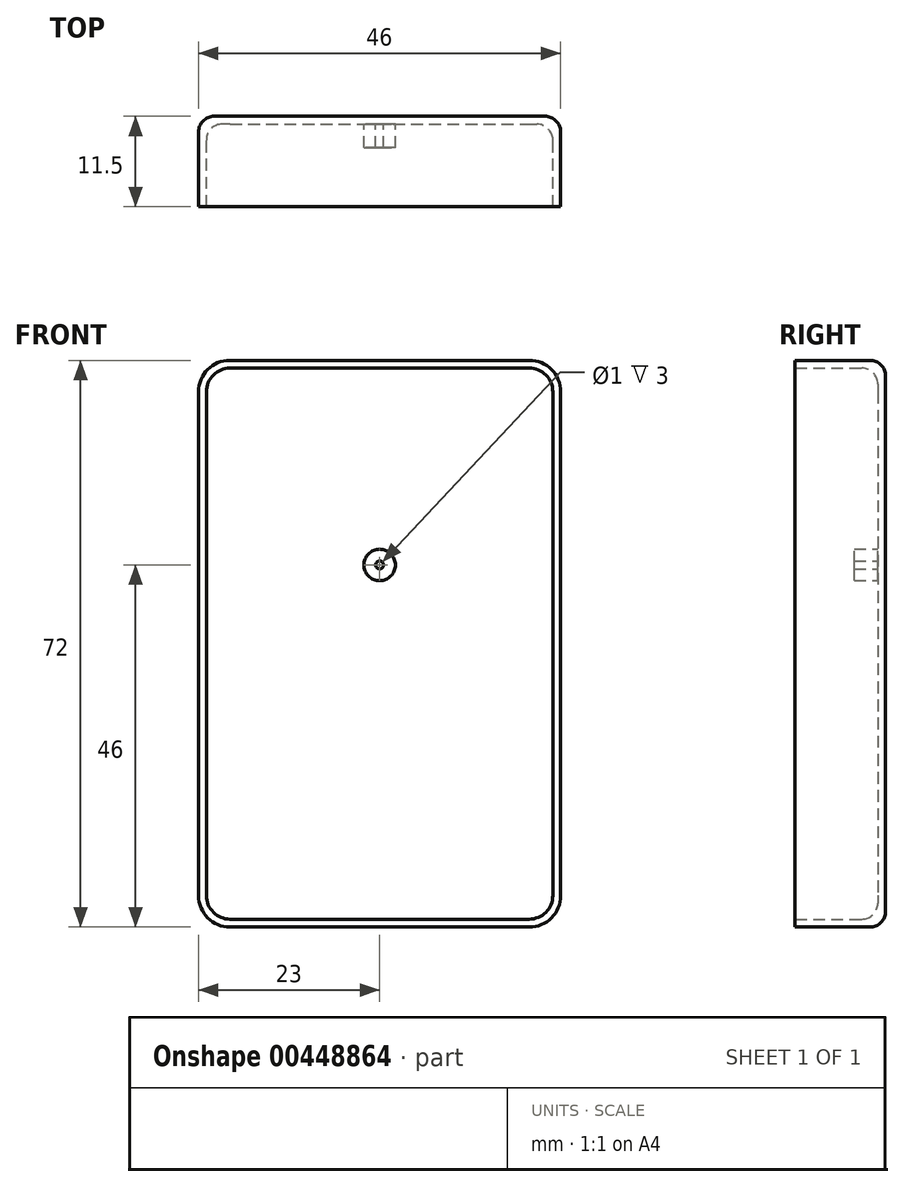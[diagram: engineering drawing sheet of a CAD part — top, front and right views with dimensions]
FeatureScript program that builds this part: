
annotation { "Feature Type Name" : "Feature", "Feature Type Description" : "" }
export const myFeature = defineFeature(function(context is Context, id is Id, definition is map)
    precondition{}
    {
        {
            var Q0;
            Q0=qCreatedBy(makeId("Front.planeOp"),FACE);
            var sketch = newSketch(context, id + "F0", { "sketchPlane" : qUnion([Q0])});
            skLineSegment(sketch, "E0.bottom", {"start": v(-19, 36) * mm, "end": v(19, 36) * mm});
            skLineSegment(sketch, "E0.top", {"start": v(-19, -36) * mm, "end": v(19, -36) * mm});
            skLineSegment(sketch, "E0.left", {"start": v(-23, 32) * mm, "end": v(-23, -32) * mm});
            skLineSegment(sketch, "E0.right", {"start": v(23, 32) * mm, "end": v(23, -32) * mm});
            skPoint(sketch, "E0.middle", {"position": v(0, 0) * mm});
            skPoint(sketch, "E1.visualSharp", {"position": v(23, 36) * mm});
            skArc(sketch, "E1.filletArc", {"start": v(23, 32) * mm, "mid": v(21.83, 34.83) * mm, "end": v(19, 36) * mm});
            skPoint(sketch, "E2.visualSharp", {"position": v(-23, 36) * mm});
            skArc(sketch, "E2.filletArc", {"start": v(-19, 36) * mm, "mid": v(-21.83, 34.83) * mm, "end": v(-23, 32) * mm});
            skPoint(sketch, "E3.visualSharp", {"position": v(-23, -36) * mm});
            skArc(sketch, "E3.filletArc", {"start": v(-23, -32) * mm, "mid": v(-21.83, -34.83) * mm, "end": v(-19, -36) * mm});
            skPoint(sketch, "E4.visualSharp", {"position": v(23, -36) * mm});
            skArc(sketch, "E4.filletArc", {"start": v(19, -36) * mm, "mid": v(21.83, -34.83) * mm, "end": v(23, -32) * mm});
            skSolve(sketch);
        }
        {
            var Q0;
            Q0=makeQuery(id+"F0.imprint","IMPRINT",FACE,{"disambiguationData":[TD([[makeQuery(id+"F0.imprint","IMPRINT",EDGE,{"derivedFrom":sQuery(id+"F0.wireOp",EDGE,"E0.bottom")}),-1.0]])]});
            extrude(context, id + "F1", {"entities" : qUnion([Q0]), "depth" : 11.5 * mm});
        }
        {
            var Q0;
            Q0=makeQuery(id+"F1.opExtrude","CAP_FACE",FACE,{"disambiguationData":[OSD([sQuery(id+"F0.wireOp",EDGE,"E0.bottom"),sQuery(id+"F0.wireOp",EDGE,"E0.top"),sQuery(id+"F0.wireOp",EDGE,"E0.left"),sQuery(id+"F0.wireOp",EDGE,"E0.right"),sQuery(id+"F0.wireOp",EDGE,"E1.filletArc"),sQuery(id+"F0.wireOp",EDGE,"E2.filletArc"),sQuery(id+"F0.wireOp",EDGE,"E3.filletArc"),sQuery(id+"F0.wireOp",EDGE,"E4.filletArc")])],"isStart":false});
            shell(context, id + "F2", {"entities" : qUnion([Q0]), "thickness" : 1 * mm});
        }
        {
            var Q0;
            Q0=qCreatedBy(makeId("Front.planeOp"),FACE);
            var sketch = newSketch(context, id + "F3", { "sketchPlane" : qUnion([Q0])});
            skCircle(sketch, "E5", {"center": v(0, 10) * mm, "radius": 2 * mm});
            skCircle(sketch, "E6", {"center": v(0, 10) * mm, "radius": 0.5 * mm});
            skSolve(sketch);
        }
        {
            var Q0;
            Q0 = qSketchRegion(id + "F3", true);
            extrude(context, id + "F4", {"entities" : qUnion([Q0]), "operationType" : NewBodyOperationType.ADD, "depth" : 4 * mm});
        }
        {
            var Q0;
            Q0=makeQuery(id+"F1.opExtrude","CAP_EDGE",EDGE,{"disambiguationData":[OSD([sQuery(id+"F0.wireOp",EDGE,"E0.right")])],"isStart":true});
            var Q1;
            {var subQ0=sQuery(id+"F0.wireOp",EDGE,"E0.left");Q1=makeQuery(id+"F2.opShell","OFFSET_EDGE",EDGE,{"disambiguationData":[OSD([subQ0]),TDD([makeQuery(id+"F1.opExtrude","CAP_EDGE",EDGE,{"disambiguationData":[OSD([subQ0])],"isStart":true})])]});}
            fillet(context, id + "F5", {"entities" : qUnion([Q0, Q1]), "radius" : 2 * mm, "tangentPropagation" : true, "allowEdgeOverflow" : false});
        }
    });
